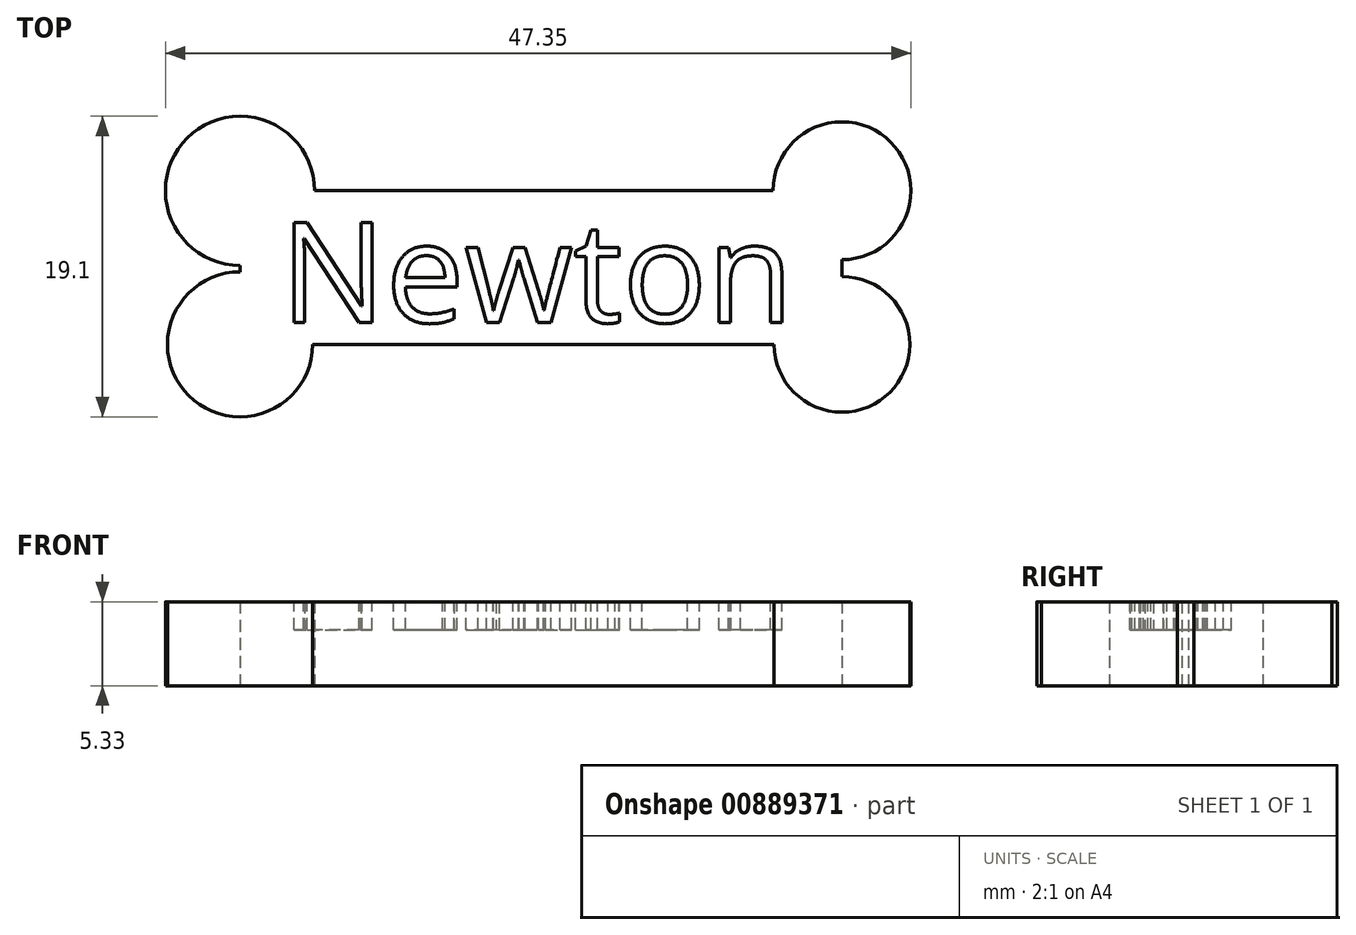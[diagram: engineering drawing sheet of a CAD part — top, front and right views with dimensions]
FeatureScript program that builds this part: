
annotation { "Feature Type Name" : "Feature", "Feature Type Description" : "" }
export const myFeature = defineFeature(function(context is Context, id is Id, definition is map)
    precondition{}
    {
        {
            var Q0;
            Q0=qCreatedBy(makeId("Top.planeOp"),FACE);
            var sketch = newSketch(context, id + "F0", { "sketchPlane" : qUnion([Q0])});
            skLineSegment(sketch, "E0.bottom", {"start": v(0, 0) * mm, "end": v(-38.23, 0) * mm});
            skLineSegment(sketch, "E0.top", {"start": v(0, -9.75) * mm, "end": v(-38.23, -9.75) * mm});
            skLineSegment(sketch, "E0.left", {"start": v(0, 0) * mm, "end": v(0, -9.75) * mm});
            skLineSegment(sketch, "E0.right", {"start": v(-38.23, 0) * mm, "end": v(-38.23, -9.75) * mm});
            skCircle(sketch, "E1", {"center": v(-38.23, 0) * mm, "radius": 4.74 * mm});
            skCircle(sketch, "E2", {"center": v(-38.23, -9.75) * mm, "radius": 4.6 * mm});
            skCircle(sketch, "E3", {"center": v(0, 0) * mm, "radius": 4.38 * mm});
            skCircle(sketch, "E4", {"center": v(0, -9.75) * mm, "radius": 4.3 * mm});
            skSolve(sketch);
        }
        {
            var Q0;
            Q0 = qSketchRegion(id + "F0", true);
            extrude(context, id + "F1", {"entities" : qUnion([Q0]), "depth" : 5.33 * mm, "offsetDistance" : 25.4 * mm});
        }
        {
            var Q0;
            Q0=makeQuery(id+"F1.opExtrude","CAP_FACE",FACE,{"disambiguationData":[OSD([sQuery(id+"F0.wireOp",EDGE,"E0.bottom"),sQuery(id+"F0.wireOp",EDGE,"E0.top"),sQuery(id+"F0.wireOp",EDGE,"E0.left"),sQuery(id+"F0.wireOp",EDGE,"E0.right"),sQuery(id+"F0.wireOp",EDGE,"E1"),sQuery(id+"F0.wireOp",EDGE,"E2"),sQuery(id+"F0.wireOp",EDGE,"E3"),sQuery(id+"F0.wireOp",EDGE,"E4")])],"isStart":false});
            var sketch = newSketch(context, id + "F2", { "sketchPlane" : qUnion([Q0])});
            skText(sketch, "E5", { "text": "Newton", "fontName": "OpenSans-Regular.ttf"});
            const initialGuessF2  = {"E5": [-0.03567, -0.00836, 1, 0, 0.0064]};
            skSetInitialGuess(sketch, initialGuessF2);
            skSolve(sketch);
        }
        {
            var Q0;
            Q0 = qSketchRegion(id + "F2", true);
            extrude(context, id + "F3", {"entities" : qUnion([Q0]), "operationType" : NewBodyOperationType.REMOVE, "oppositeDirection" : true, "depth" : 1.78 * mm, "offsetDistance" : 25.4 * mm});
        }
    });
